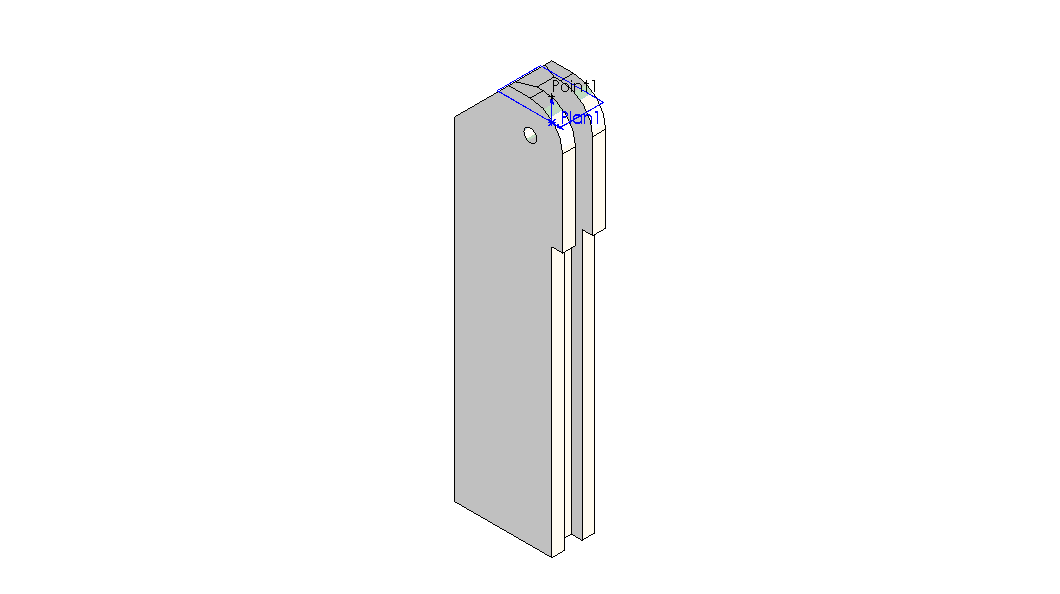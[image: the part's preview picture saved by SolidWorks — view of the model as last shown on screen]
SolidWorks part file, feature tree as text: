
SOLIDWORKS PART (.sldprt)
format: sldprt  version: not decoded by parser v0  size: 172,544 bytes
history: native  units: mm
features: plane x4, sketch x4, extrude x2, cut_extrude x2, material x1, chamfer x1 (+8 scaffold rows collapsed)
feature tree (22):
  scaffold x8  (default folders/planes/origin — collapsed)
  material  "Matériau <non spécifié>"
  plane  "Plan de face"
  plane  "Plan de dessus"
  plane  "Plan de droite"
  sketch  "Esquisse1"  dims[c1.D1=6.0mm c1.D7=15.0mm c1.D2=50.0mm c1.D3=10.0mm c1.D4=~108.091853mm c2.D4=45.0deg c2.D5=5.0mm c2.D6=15.0mm c2.D8=125.0mm c2.D9=~108.091853mm c3.D9=30.0deg c3.D10=51.85mm c3.D11=12.0mm c3.D12=15.0mm]
  extrude  "Extrusion1"  Depth=10mm
  sketch  "Esquisse2"  dims[D1=8.0mm D2=4.0mm D3=30.0mm]
  cut_extrude  "Enlèv. mat.-Extru.2"  [1 undecoded]
  chamfer  "Chanfrein1"  Distance=5mm Angle=30deg
  sketch  "Esquisse3"  dims[D1=10.0mm]
  cut_extrude  "Enlèv. mat.-Extru.3"  [1 undecoded]
  plane  "Plan1"  Offset=4.5mm
  sketch  "Esquisse4"  dims[D1=1.0mm]
  extrude  "Extrusion2"  Depth=0.5mm
decode coverage: 7 of 9 modeling features carry decoded parameters
note: ~ marks probable driven/reference dimensions
note: 2 parameter values undecoded
note: suppression state not decoded; provenance and decode notes live in map.json
